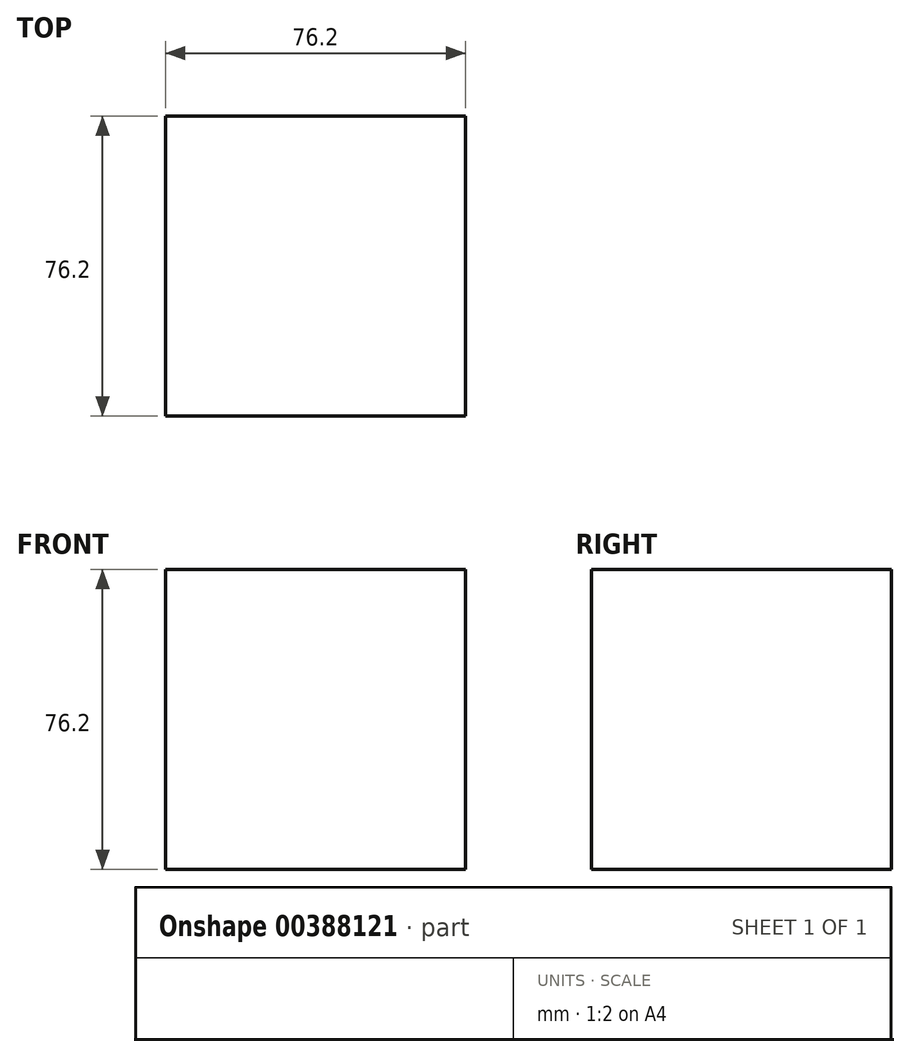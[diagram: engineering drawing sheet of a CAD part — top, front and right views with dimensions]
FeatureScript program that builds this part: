
annotation { "Feature Type Name" : "Feature", "Feature Type Description" : "" }
export const myFeature = defineFeature(function(context is Context, id is Id, definition is map)
    precondition{}
    {
        {
            var Q0;
            Q0=qCreatedBy(makeId("Front.planeOp"),FACE);
            var sketch = newSketch(context, id + "F0", { "sketchPlane" : qUnion([Q0])});
            skLineSegment(sketch, "E0.bottom", {"start": v(-32.7, 37.82) * mm, "end": v(43.5, 37.82) * mm});
            skLineSegment(sketch, "E0.top", {"start": v(-32.7, -38.38) * mm, "end": v(43.5, -38.38) * mm});
            skLineSegment(sketch, "E0.left", {"start": v(-32.7, 37.82) * mm, "end": v(-32.7, -38.38) * mm});
            skLineSegment(sketch, "E0.right", {"start": v(43.5, 37.82) * mm, "end": v(43.5, -38.38) * mm});
            skSolve(sketch);
        }
        {
            var Q0;
            Q0=makeQuery(id+"F0.imprint","IMPRINT",FACE,{"disambiguationData":[TD([[makeQuery(id+"F0.imprint","IMPRINT",EDGE,{"derivedFrom":sQuery(id+"F0.wireOp",EDGE,"E0.bottom")}),-1.0]])]});
            extrude(context, id + "F1", {"entities" : qUnion([Q0]), "depth" : 76.2 * mm});
        }
    });
